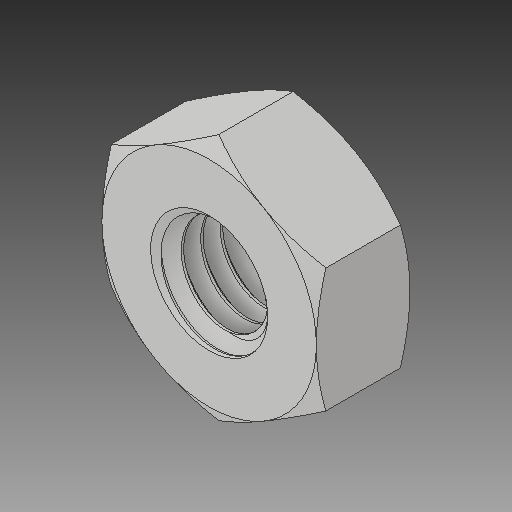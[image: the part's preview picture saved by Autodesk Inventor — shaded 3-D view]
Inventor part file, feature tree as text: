
AUTODESK INVENTOR PART (.ipt)
format: ipt  version: 2019.4 (Build 234330000, 330)  size: 316,928 bytes
history: native  units: in
note: dims shown in document units (in); Inventor stores cm internally (conversion verified against a paired STEP export)
features: mirror x1
ambient origin geometry x8: Origin, YZ Plane, XZ Plane, XY Plane, X Axis, Y Axis, Z Axis, Center Point
bodies: Solid1 (feature_tree)
feature tree (1):
  mirror  "Mirror2"
